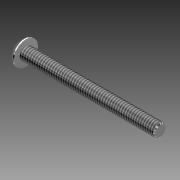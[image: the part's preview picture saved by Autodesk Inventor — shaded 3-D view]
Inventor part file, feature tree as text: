
AUTODESK INVENTOR PART (.ipt)
format: ipt  version: 2011 (Build 150239000, 239)  size: 104,960 bytes
history: native  units: in
note: dims shown in document units (in); Inventor stores cm internally (conversion verified against a paired STEP export)
features: other x1, imported_body x1, thread x1
ambient origin geometry x8: Origin, YZ Plane, XZ Plane, XY Plane, X Axis, Y Axis, Z Axis, Center Point
feature tree (3):
  parser-record x1  (decoder bookkeeping rows leaked as tree rows — omitted from the tree; the rows remain in map.json)
  imported_body  "Base1"
  thread  "Thread1"  [1 undecoded]
note: 1 required parameter value undecoded (feature->parameter linkage not recoverable at this tier; creation-order binding heuristic only, values carry confidence <= 0.55)
